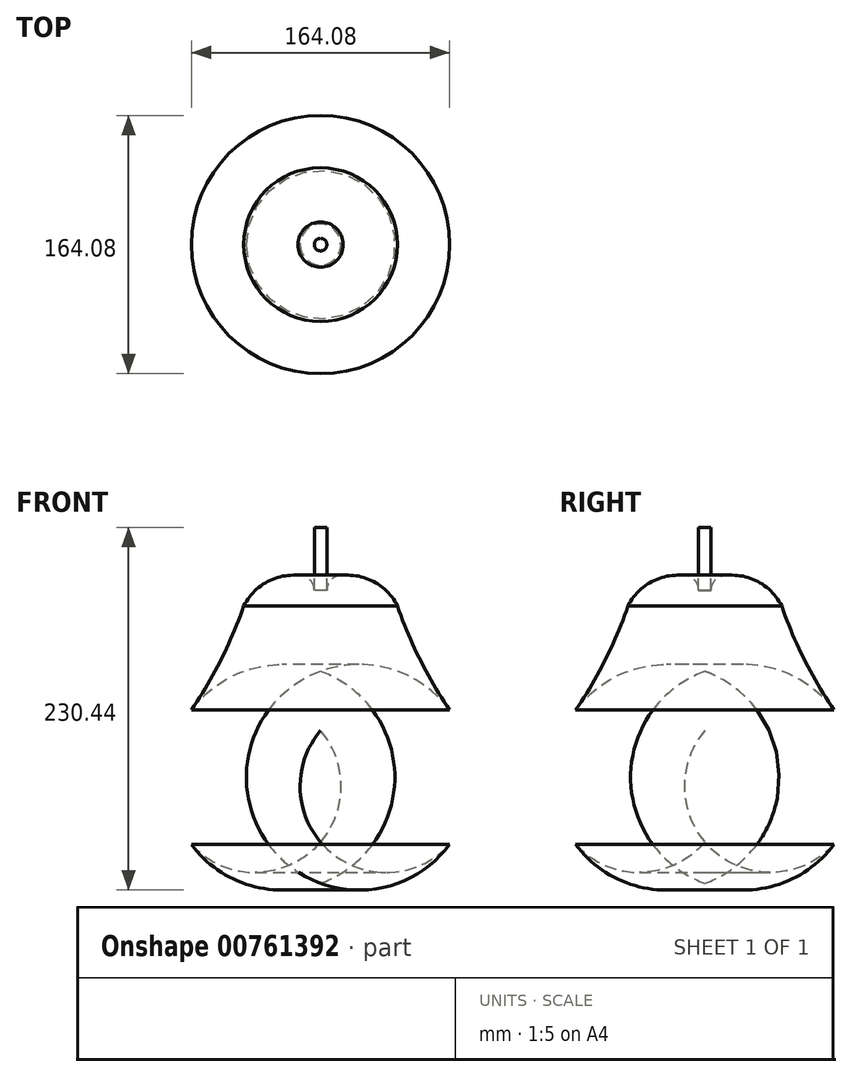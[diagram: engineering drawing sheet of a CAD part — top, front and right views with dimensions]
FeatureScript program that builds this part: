
annotation { "Feature Type Name" : "Feature", "Feature Type Description" : "" }
export const myFeature = defineFeature(function(context is Context, id is Id, definition is map)
    precondition{}
    {
        {
            var Q0;
            Q0=qCreatedBy(makeId("Front.planeOp"),FACE);
            var sketch = newSketch(context, id + "F0", { "sketchPlane" : qUnion([Q0])});
            skLineSegment(sketch, "E0", {"start": v(0, 105.75) * mm, "end": v(0, -94.25) * mm});
            skLineSegment(sketch, "E1", {"start": v(0, 105.75) * mm, "end": v(4, 105.75) * mm});
            skLineSegment(sketch, "E2", {"start": v(4, 105.75) * mm, "end": v(4, 65.75) * mm});
            skArc(sketch, "E3", {"start": v(14.36, 75.21) * mm, "mid": v(7.1, 72.76) * mm, "end": v(4, 65.75) * mm});
            skArc(sketch, "E4", {"start": v(48.8, 55.75) * mm, "mid": v(34.57, 70.79) * mm, "end": v(14.36, 75.21) * mm});
            skArc(sketch, "E5", {"start": v(48.8, 55.75) * mm, "mid": v(63.22, 21.57) * mm, "end": v(82.04, -10.4) * mm});
            skArc(sketch, "E6", {"start": v(82.04, -95.7) * mm, "mid": v(96.12, -53.05) * mm, "end": v(82.04, -10.4) * mm});
            skArc(sketch, "E7", {"start": v(0, -94.25) * mm, "mid": v(40.7, -113.5) * mm, "end": v(82.04, -95.7) * mm});
            skSolve(sketch);
        }
        {
            var Q0;
            Q0 = qSketchRegion(id + "F0", true);
            var Q1;
            Q1=sQuery(id+"F0.wireOp",EDGE,"E0");
            revolve(context, id + "F1", {"surfaceOperationType" : NewSurfaceOperationType.NEW, "entities" : qUnion([Q0]), "axis" : qUnion([Q1]), "revolveType" : RevolveType.FULL});
        }
    });
